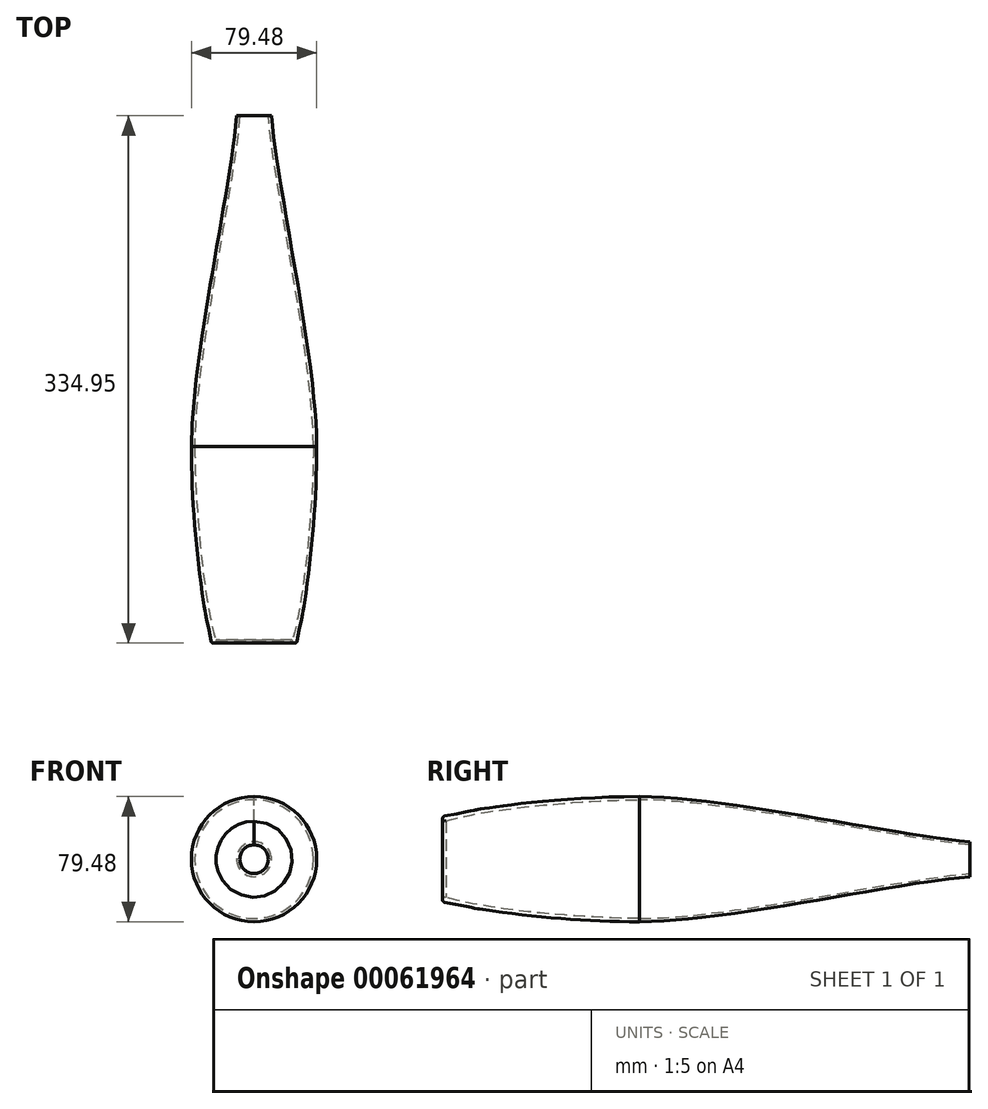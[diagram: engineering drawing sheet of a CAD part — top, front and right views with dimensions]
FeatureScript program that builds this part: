
annotation { "Feature Type Name" : "Feature", "Feature Type Description" : "" }
export const myFeature = defineFeature(function(context is Context, id is Id, definition is map)
    precondition{}
    {
        {
            var Q0;
            Q0=qCreatedBy(makeId("Top.planeOp"),FACE);
            var sketch = newSketch(context, id + "F0", { "sketchPlane" : qUnion([Q0])});
            skLineSegment(sketch, "E0", {"start": v(0, 334.95) * mm, "end": v(0, 0) * mm, "construction": true});
            skLineSegment(sketch, "E1", {"start": v(0, 334.95) * mm, "end": v(11.11, 334.95) * mm, "construction": true});
            skLineSegment(sketch, "E2", {"start": v(0, 0) * mm, "end": v(27.11, 0) * mm, "construction": true});
            skLineSegment(sketch, "E3", {"start": v(0, 24) * mm, "end": v(31.75, 24) * mm, "construction": true});
            skLineSegment(sketch, "E4", {"start": v(0, 124.97) * mm, "end": v(39.74, 124.97) * mm, "construction": true});
            skLineSegment(sketch, "E5", {"start": v(0, 287.26) * mm, "end": v(14.92, 287.26) * mm, "construction": true});
            skFitSpline(sketch, "E6", {"points": [v(11.11, 334.95) * mm, v(39.74, 124.97) * mm], "startDerivative": vector(11.43, -143.07) * mm, "endDerivative": vector(0, -167.5) * mm});
            skLineSegment(sketch, "E7", {"start": v(39.74, 124.97) * mm, "end": v(39.74, 180.8) * mm, "construction": true});
            skLineSegment(sketch, "E8", {"start": v(39.74, 124.97) * mm, "end": v(39.74, 73.94) * mm, "construction": true});
            skFitSpline(sketch, "E9", {"points": [v(39.74, 124.97) * mm, v(31.6, 23.09) * mm, v(27.11, 0) * mm], "startDerivative": vector(0, -226.52) * mm, "endDerivative": vector(-42.9, -222.12) * mm});
            skLineSegment(sketch, "E10", {"start": v(31.77, 24.1) * mm, "end": v(27.11, 0) * mm, "construction": true});
            skArc(sketch, "E11", {"start": v(24.22, 2.13) * mm, "mid": v(25.36, 0.05) * mm, "end": v(27.37, 1.32) * mm});
            skFitSpline(sketch, "E12", {"points": [v(23.48, 0) * mm, v(37.7, 124.97) * mm], "startDerivative": vector(26.19, 71.95) * mm, "endDerivative": vector(0, 99.04) * mm});
            skFitSpline(sketch, "E13", {"points": [v(9.08, 334.95) * mm, v(37.7, 124.97) * mm], "startDerivative": vector(11.83, -143.07) * mm, "endDerivative": vector(0, -169.24) * mm});
            skLineSegment(sketch, "E14", {"start": v(37.7, 124.97) * mm, "end": v(37.7, 181.38) * mm, "construction": true});
            skLineSegment(sketch, "E15", {"start": v(37.7, 124.97) * mm, "end": v(37.7, 75.05) * mm, "construction": true});
            skLineSegment(sketch, "E16", {"start": v(9.08, 334.95) * mm, "end": v(11.11, 334.95) * mm});
            skSolve(sketch);
        }
        {
            var Q0;
            Q0=makeQuery(id+"F0.imprint","IMPRINT",FACE,{"disambiguationData":[TD([[makeQuery(id+"F0.imprint","IMPRINT",EDGE,{"derivedFrom":sQuery(id+"F0.wireOp",EDGE,"E6")}),-1.0]])]});
            var Q1;
            Q1=sQuery(id+"F0.wireOp",EDGE,"E0");
            revolve(context, id + "F1", {"entities" : qUnion([Q0]), "axis" : qUnion([Q1]), "revolveType" : RevolveType.FULL});
        }
    });
